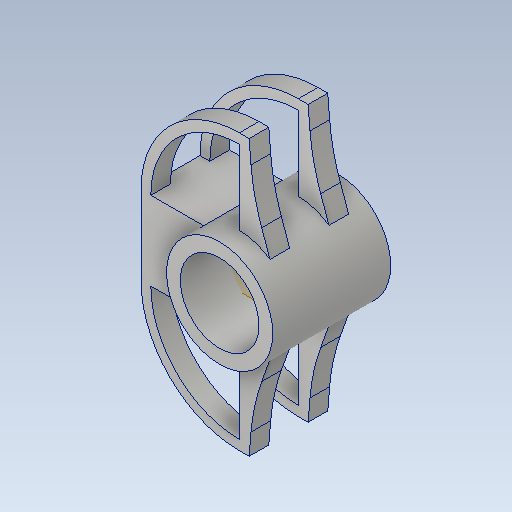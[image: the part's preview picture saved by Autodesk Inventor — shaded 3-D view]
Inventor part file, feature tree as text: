
AUTODESK INVENTOR PART (.ipt)
format: ipt  version: 2021 (Build 250183000, 183)  size: 230,400 bytes
history: native  units: mm
features: sketch x7, extrude x4, mirror x2, plane x1, direct_edit x1, other x1
ambient origin geometry x8: Origin, YZ Plane, XZ Plane, XY Plane, X Axis, Y Axis, Z Axis, Center Point
bodies: Solid1 (feature_tree)
feature tree (16):
  sketch  "Sketch1"  dims[d0=40.0mm d1=54.0mm]
  sketch  "Sketch2"  dims[d2=23.0mm d3=50.0mm]
  sketch  "Sketch3"  dims[d4=40.0mm d5=20.0mm]
  extrude  "Extrusion1"  Depth=54.0mm
  extrude  "Extrusion2"  Depth=50.0mm
  extrude  "Extrusion3"  Depth=20.0mm
  sketch  "Sketch6"  dims[d10=54.0mm]
  plane  "Work Plane1"
  extrude  "Extrusion4"  Depth=40.0mm TaperAngle=0.0deg
  mirror  "Mirror1"
  mirror  "Mirror2"
  direct_edit  "Direct Edit1"
  sketch  "Sketch4"  dims[d6=20.0mm d7=40.0mm d8=0.0mm]
  sketch  "Sketch5"  dims[d9=40.0mm]
  sketch  "Sketch7"  dims[d11=10.0mm d12=0.0mm d13=40.0mm d14=54.0mm d15=10.0mm d16=0.0mm d17=10.0mm d18=50.0mm d19=45.0mm d20=38.0mm d21=5.0mm d22=5.0mm d23=31.56663mm d24=16.570637mm d25=29.795722mm d26=28.855136mm d27=22.105665mm d28=100.0mm d29=10.0mm d30=0.0mm d31=20.0mm d32=10.0mm d33=10.0mm]
  other  "Scale1"
